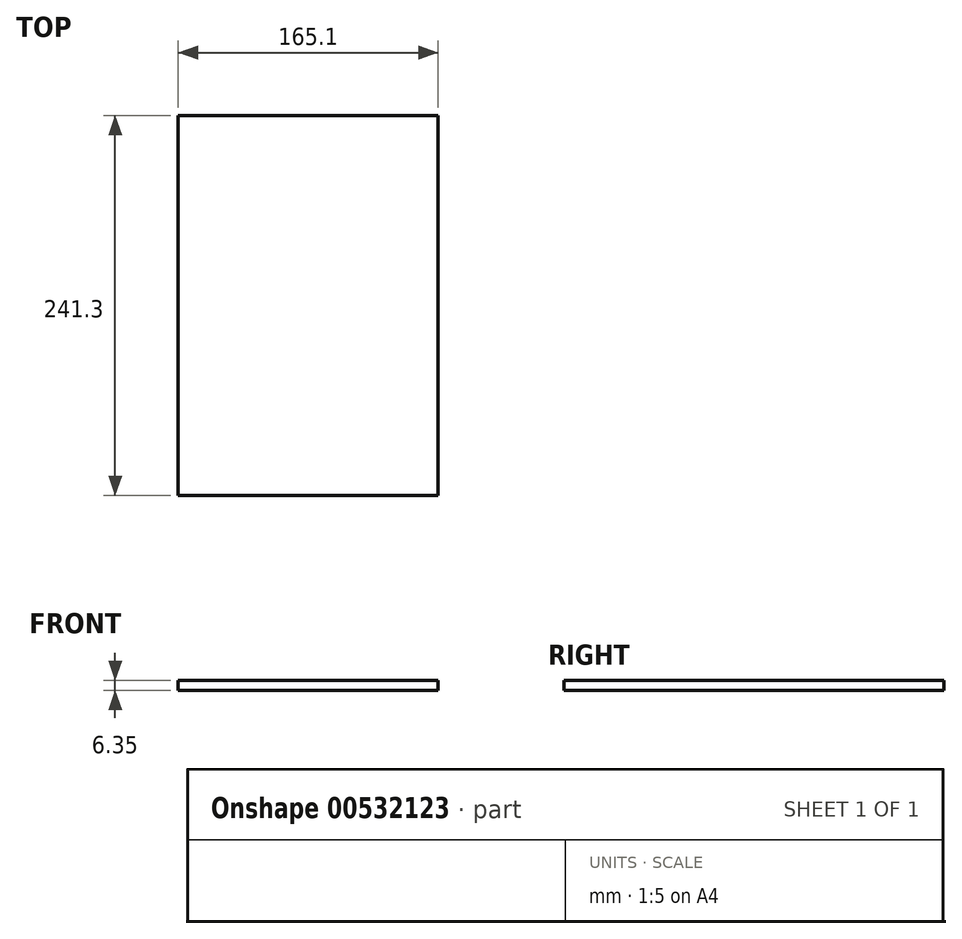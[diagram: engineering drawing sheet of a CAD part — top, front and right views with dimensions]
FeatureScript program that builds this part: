
annotation { "Feature Type Name" : "Feature", "Feature Type Description" : "" }
export const myFeature = defineFeature(function(context is Context, id is Id, definition is map)
    precondition{}
    {
        {
            var Q0;
            Q0=qCreatedBy(makeId("Top.planeOp"),FACE);
            var sketch = newSketch(context, id + "F0", { "sketchPlane" : qUnion([Q0])});
            skLineSegment(sketch, "E0.bottom", {"start": v(82.55, -120.65) * mm, "end": v(-82.55, -120.65) * mm});
            skLineSegment(sketch, "E0.top", {"start": v(82.55, 120.65) * mm, "end": v(-82.55, 120.65) * mm});
            skLineSegment(sketch, "E0.left", {"start": v(82.55, -120.65) * mm, "end": v(82.55, 120.65) * mm});
            skLineSegment(sketch, "E0.right", {"start": v(-82.55, -120.65) * mm, "end": v(-82.55, 120.65) * mm});
            skPoint(sketch, "E0.middle", {"position": v(0, 0) * mm});
            skSolve(sketch);
        }
        {
            var Q0;
            Q0 = qSketchRegion(id + "F0", true);
            extrude(context, id + "F1", {"entities" : qUnion([Q0]), "depth" : 6.35 * mm, "offsetDistance" : 25.4 * mm});
        }
    });
